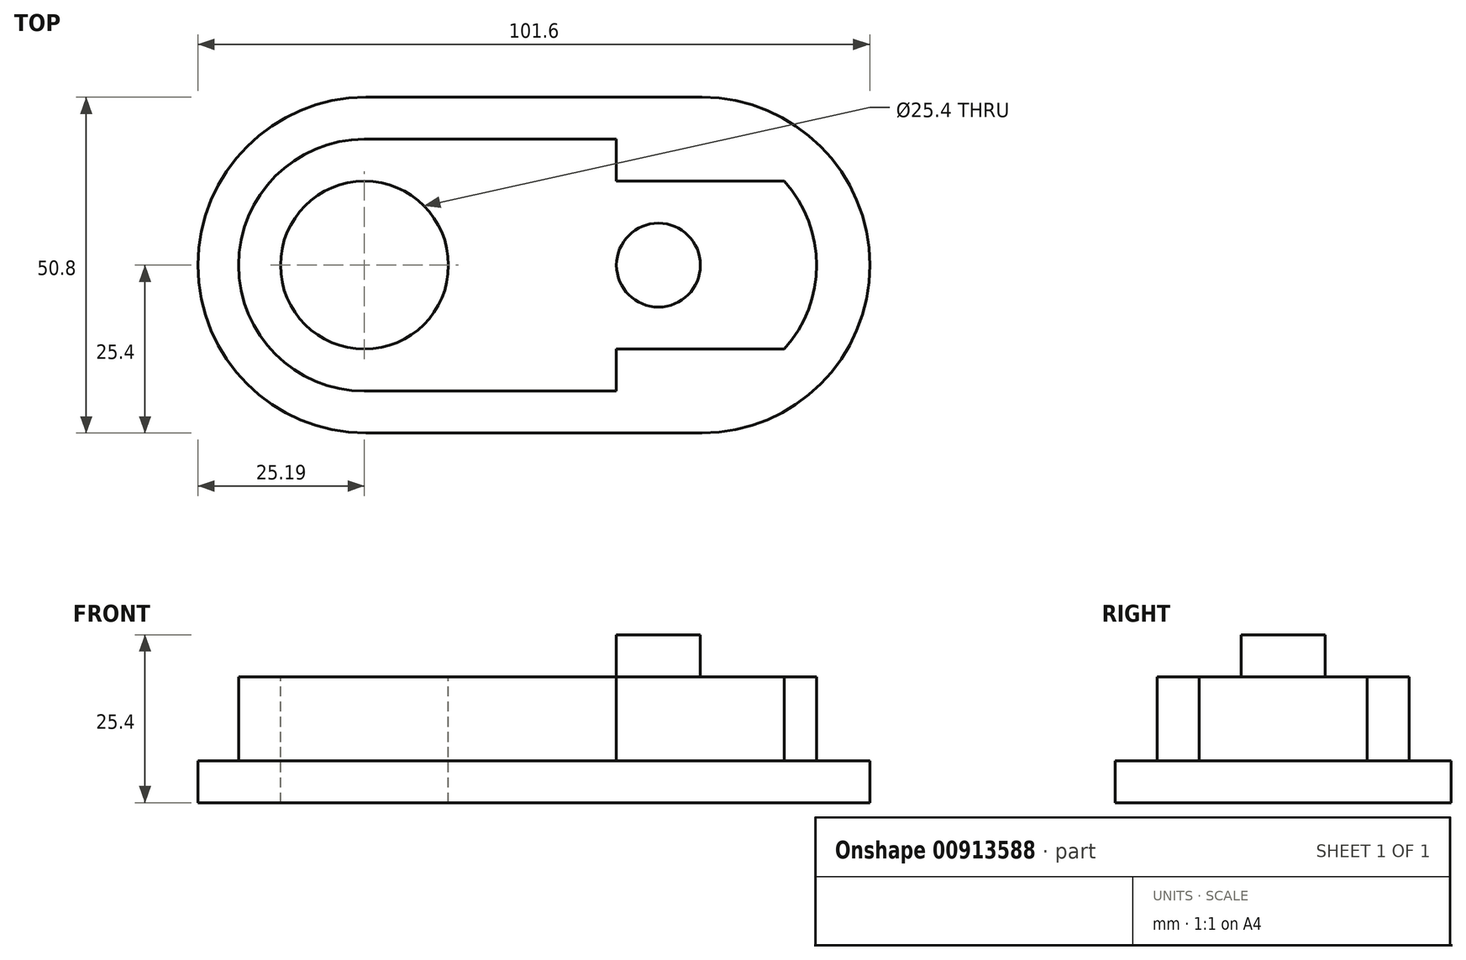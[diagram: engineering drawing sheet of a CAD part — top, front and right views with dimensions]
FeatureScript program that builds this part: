
annotation { "Feature Type Name" : "Feature", "Feature Type Description" : "" }
export const myFeature = defineFeature(function(context is Context, id is Id, definition is map)
    precondition{}
    {
        {
            var Q0;
            Q0=qCreatedBy(makeId("Top.planeOp"),FACE);
            var sketch = newSketch(context, id + "F0", { "sketchPlane" : qUnion([Q0])});
            skLineSegment(sketch, "E0.bottom", {"start": v(0, -19.05) * mm, "end": v(-38.1, -19.05) * mm});
            skLineSegment(sketch, "E0.top", {"start": v(0, 19.05) * mm, "end": v(-38.1, 19.05) * mm});
            skLineSegment(sketch, "E0.left", {"start": v(0, -19.05) * mm, "end": v(0, -12.7) * mm});
            skLineSegment(sketch, "E1.bottom", {"start": v(0, 12.7) * mm, "end": v(25.4, 12.7) * mm});
            skLineSegment(sketch, "E1.top", {"start": v(0, -12.7) * mm, "end": v(25.4, -12.7) * mm});
            skLineSegment(sketch, "E2.trimOffspring", {"start": v(0, 12.7) * mm, "end": v(0, 19.05) * mm});
            skArc(sketch, "E3", {"start": v(-38.1, 19.05) * mm, "mid": v(-57.15, 0) * mm, "end": v(-38.1, -19.05) * mm});
            skArc(sketch, "E4", {"start": v(25.4, -12.7) * mm, "mid": v(30.25, 0) * mm, "end": v(25.4, 12.7) * mm});
            skSolve(sketch);
        }
        {
            var Q0;
            Q0=makeQuery(id+"F0.imprint","IMPRINT",FACE,{"disambiguationData":[TD([[makeQuery(id+"F0.imprint","IMPRINT",EDGE,{"derivedFrom":sQuery(id+"F0.wireOp",EDGE,"E0.bottom")}),-1.0]])]});
            extrude(context, id + "F1", {"entities" : qUnion([Q0]), "depth" : 12.7 * mm, "offsetDistance" : 25.4 * mm});
        }
        {
            var Q0;
            Q0=makeQuery(id+"F1.opExtrude","CAP_FACE",FACE,{"disambiguationData":[OSD([sQuery(id+"F0.wireOp",EDGE,"E0.bottom"),sQuery(id+"F0.wireOp",EDGE,"E0.top"),sQuery(id+"F0.wireOp",EDGE,"E0.left"),sQuery(id+"F0.wireOp",EDGE,"E1.bottom"),sQuery(id+"F0.wireOp",EDGE,"E1.top"),sQuery(id+"F0.wireOp",EDGE,"E2.trimOffspring"),sQuery(id+"F0.wireOp",EDGE,"E3"),sQuery(id+"F0.wireOp",EDGE,"E4")])],"isStart":false});
            var sketch = newSketch(context, id + "F2", { "sketchPlane" : qUnion([Q0])});
            skCircle(sketch, "E5", {"center": v(-38.1, 0) * mm, "radius": 12.7 * mm});
            skCircle(sketch, "E6", {"center": v(6.35, 0) * mm, "radius": 6.35 * mm});
            skPoint(sketch, "E7", {"position": v(12.7, 0) * mm});
            skSolve(sketch);
        }
        {
            var Q0;
            Q0=makeQuery(id+"F1.opExtrude","CAP_FACE",FACE,{"disambiguationData":[OSD([sQuery(id+"F0.wireOp",EDGE,"E0.bottom"),sQuery(id+"F0.wireOp",EDGE,"E0.top"),sQuery(id+"F0.wireOp",EDGE,"E0.left"),sQuery(id+"F0.wireOp",EDGE,"E1.bottom"),sQuery(id+"F0.wireOp",EDGE,"E1.top"),sQuery(id+"F0.wireOp",EDGE,"E2.trimOffspring"),sQuery(id+"F0.wireOp",EDGE,"E3"),sQuery(id+"F0.wireOp",EDGE,"E4")])],"isStart":true});
            var sketch = newSketch(context, id + "F3", { "sketchPlane" : qUnion([Q0])});
            skArc(sketch, "E8", {"start": v(-37.89, 25.4) * mm, "mid": v(-63.29, 0) * mm, "end": v(-37.89, -25.4) * mm});
            skLineSegment(sketch, "E9", {"start": v(-37.89, 25.4) * mm, "end": v(12.91, 25.4) * mm});
            skLineSegment(sketch, "E10.MirrorCS", {"start": v(-37.89, -25.4) * mm, "end": v(12.91, -25.4) * mm});
            skArc(sketch, "E11", {"start": v(12.91, -25.4) * mm, "mid": v(38.31, 0) * mm, "end": v(12.91, 25.4) * mm});
            skSolve(sketch);
        }
        {
            var Q0;
            Q0 = qSketchRegion(id + "F3", true);
            extrude(context, id + "F4", {"entities" : qUnion([Q0]), "operationType" : NewBodyOperationType.ADD, "depth" : 6.35 * mm, "offsetDistance" : 25.4 * mm});
        }
        {
            var Q0;
            Q0=makeQuery(id+"F2.imprint","IMPRINT",FACE,{"disambiguationData":[TD([[makeQuery(id+"F2.imprint","IMPRINT",EDGE,{"derivedFrom":sQuery(id+"F2.wireOp",EDGE,"E5")}),1.0]])]});
            extrude(context, id + "F5", {"entities" : qUnion([Q0]), "operationType" : NewBodyOperationType.REMOVE, "endBound" : BoundingType.THROUGH_ALL, "oppositeDirection" : true, "depth" : 25.4 * mm, "offsetDistance" : 25.4 * mm});
        }
        {
            var Q0;
            Q0=makeQuery(id+"F2.imprint","IMPRINT",FACE,{"disambiguationData":[TD([[makeQuery(id+"F2.imprint","IMPRINT",EDGE,{"derivedFrom":sQuery(id+"F2.wireOp",EDGE,"E6")}),1.0]])]});
            var Q1;
            Q1=sQuery(id+"F2.wireOp",EDGE,"E6");
            extrude(context, id + "F6", {"entities" : qUnion([Q0]), "operationType" : NewBodyOperationType.ADD, "surfaceEntities" : qUnion([Q1]), "depth" : 6.35 * mm, "offsetDistance" : 25.4 * mm});
        }
    });
